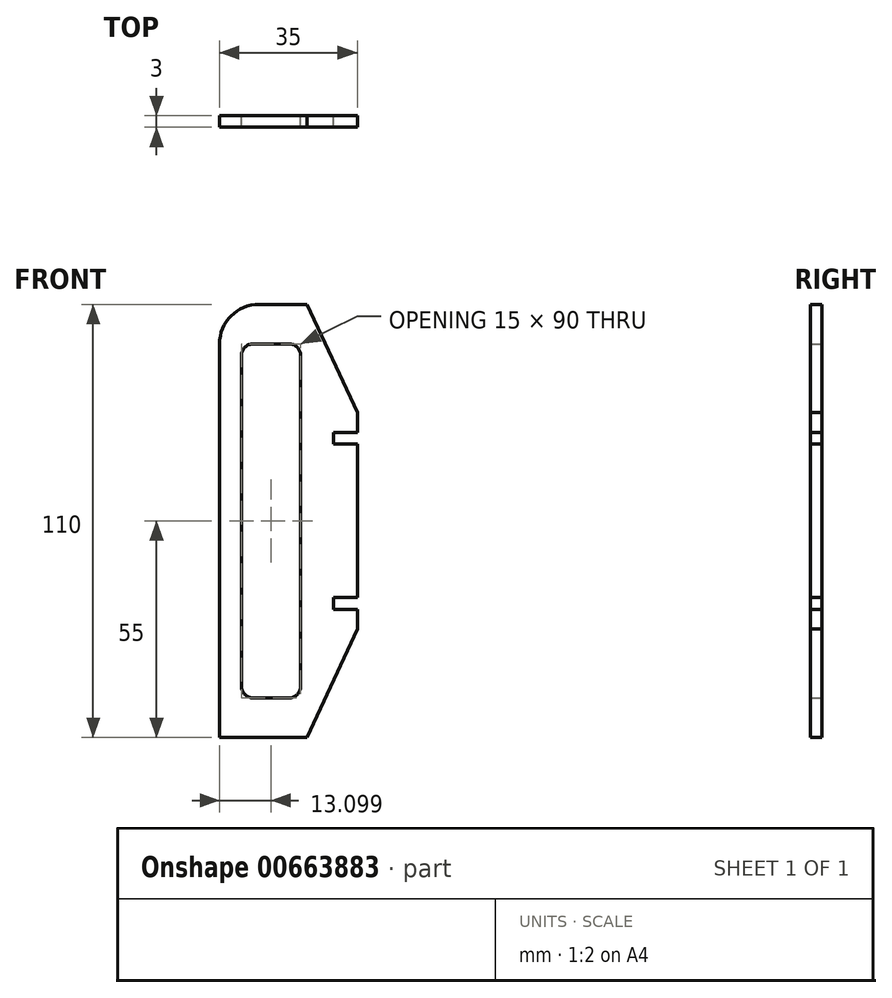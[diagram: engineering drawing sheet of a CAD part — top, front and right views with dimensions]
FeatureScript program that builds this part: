
annotation { "Feature Type Name" : "Feature", "Feature Type Description" : "" }
export const myFeature = defineFeature(function(context is Context, id is Id, definition is map)
    precondition{}
    {
        {
            var Q0;
            Q0=qCreatedBy(makeId("Front.planeOp"),FACE);
            var sketch = newSketch(context, id + "F0", { "sketchPlane" : qUnion([Q0])});
            skLineSegment(sketch, "E0.0", {"start": v(4.68, 55) * mm, "end": v(17.5, 27.5) * mm});
            skLineSegment(sketch, "E0.1", {"start": v(17.5, 27.5) * mm, "end": v(17.5, 22.5) * mm});
            skLineSegment(sketch, "E0.2", {"start": v(17.5, -27.5) * mm, "end": v(4.68, -55) * mm});
            skLineSegment(sketch, "E0.3", {"start": v(4.68, -55) * mm, "end": v(-17.5, -55) * mm});
            skLineSegment(sketch, "E0.4", {"start": v(-17.5, -55) * mm, "end": v(-17.5, 45) * mm});
            skLineSegment(sketch, "E0.5", {"start": v(-7.5, 55) * mm, "end": v(4.68, 55) * mm});
            skLineSegment(sketch, "E1.bottom", {"start": v(17.5, 22.5) * mm, "end": v(11.5, 22.5) * mm});
            skLineSegment(sketch, "E1.top", {"start": v(17.5, 19.5) * mm, "end": v(11.5, 19.5) * mm});
            skLineSegment(sketch, "E1.right", {"start": v(11.5, 22.5) * mm, "end": v(11.5, 19.5) * mm});
            skLineSegment(sketch, "E2.trimOffspring", {"start": v(17.5, 19.5) * mm, "end": v(17.5, -19.5) * mm});
            skLineSegment(sketch, "E3.MirrorCS", {"start": v(17.5, -19.5) * mm, "end": v(11.5, -19.5) * mm});
            skLineSegment(sketch, "E4.MirrorCS", {"start": v(11.5, -22.5) * mm, "end": v(11.5, -19.5) * mm});
            skLineSegment(sketch, "E5.MirrorCS", {"start": v(17.5, -22.5) * mm, "end": v(11.5, -22.5) * mm});
            skPoint(sketch, "E6.MirrorCS.start.orphan", {"position": v(17.5, -22.5) * mm});
            skLineSegment(sketch, "E7.trimOffspring", {"start": v(17.5, -22.5) * mm, "end": v(17.5, -27.5) * mm});
            skLineSegment(sketch, "E8.bottom", {"start": v(-8.9, 45) * mm, "end": v(0.1, 45) * mm});
            skLineSegment(sketch, "E8.top", {"start": v(-8.9, -45) * mm, "end": v(0.1, -45) * mm});
            skLineSegment(sketch, "E8.left", {"start": v(-11.9, 42) * mm, "end": v(-11.9, -42) * mm});
            skLineSegment(sketch, "E8.right", {"start": v(3.1, 42) * mm, "end": v(3.1, -42) * mm});
            skPoint(sketch, "E9.visualSharp", {"position": v(-17.5, 55) * mm});
            skArc(sketch, "E9.filletArc", {"start": v(-7.5, 55) * mm, "mid": v(-14.57, 52.07) * mm, "end": v(-17.5, 45) * mm});
            skPoint(sketch, "E10.visualSharp", {"position": v(-11.9, 45) * mm});
            skArc(sketch, "E10.filletArc", {"start": v(-8.9, 45) * mm, "mid": v(-11.02, 44.12) * mm, "end": v(-11.9, 42) * mm});
            skPoint(sketch, "E11.visualSharp", {"position": v(3.1, 45) * mm});
            skArc(sketch, "E11.filletArc", {"start": v(3.1, 42) * mm, "mid": v(2.22, 44.12) * mm, "end": v(0.1, 45) * mm});
            skPoint(sketch, "E12.visualSharp", {"position": v(-11.9, -45) * mm});
            skArc(sketch, "E12.filletArc", {"start": v(-11.9, -42) * mm, "mid": v(-11.02, -44.12) * mm, "end": v(-8.9, -45) * mm});
            skPoint(sketch, "E13.visualSharp", {"position": v(3.1, -45) * mm});
            skArc(sketch, "E13.filletArc", {"start": v(0.1, -45) * mm, "mid": v(2.22, -44.12) * mm, "end": v(3.1, -42) * mm});
            skSolve(sketch);
        }
        {
            var Q0;
            Q0 = qSketchRegion(id + "F0", true);
            extrude(context, id + "F1", {"entities" : qUnion([Q0]), "depth" : 3 * mm, "offsetDistance" : 25 * mm});
        }
    });
